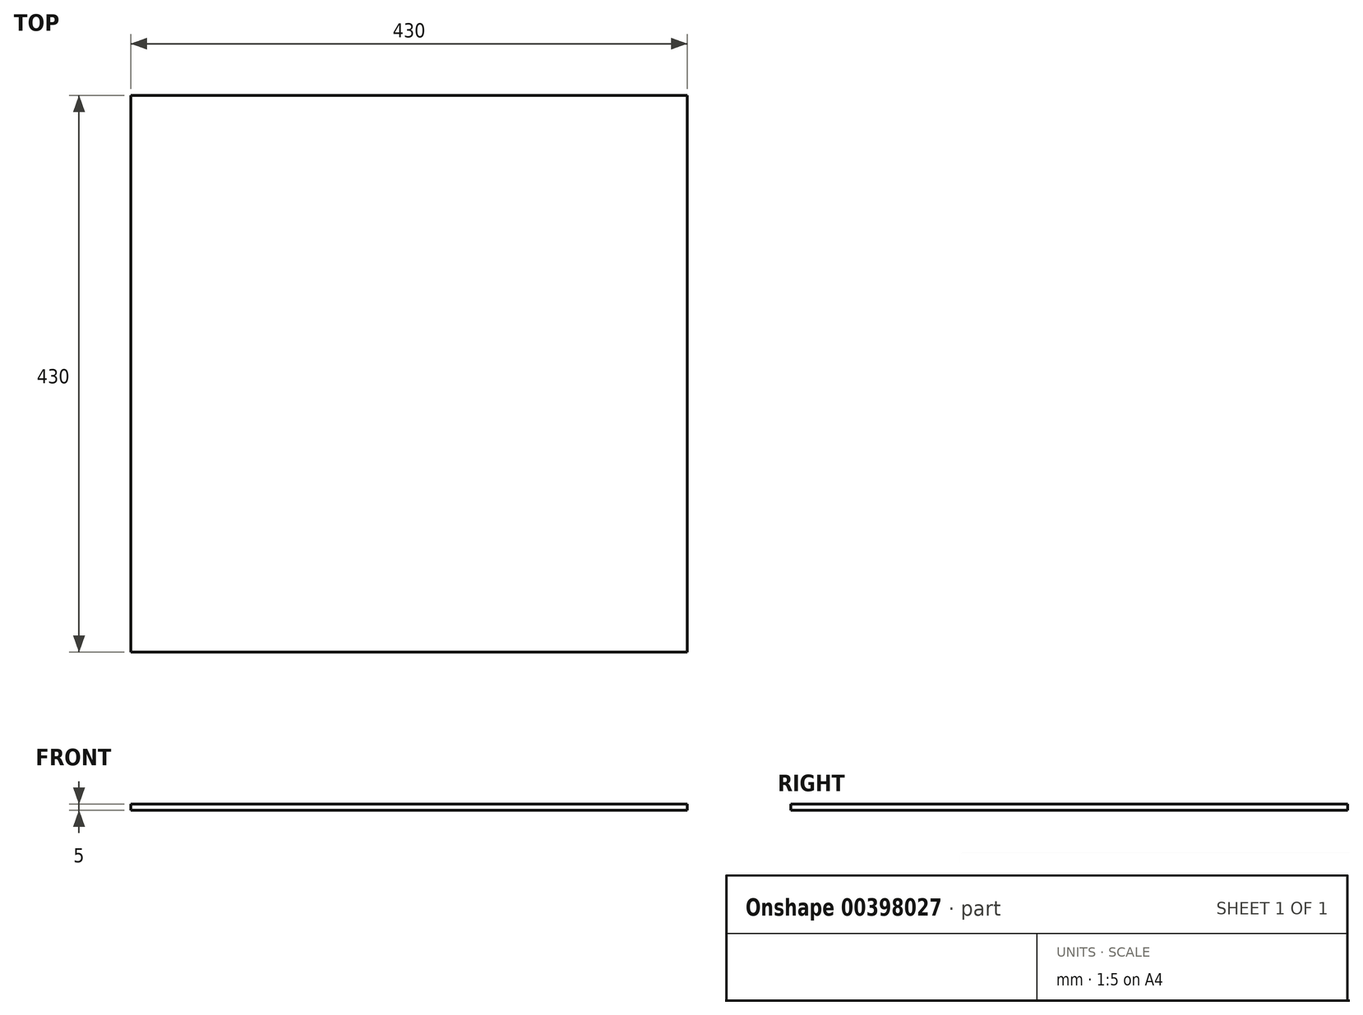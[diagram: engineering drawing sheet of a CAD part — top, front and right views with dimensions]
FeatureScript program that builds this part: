
annotation { "Feature Type Name" : "Feature", "Feature Type Description" : "" }
export const myFeature = defineFeature(function(context is Context, id is Id, definition is map)
    precondition{}
    {
        {
            var Q0;
            Q0=qCreatedBy(makeId("Top.planeOp"),FACE);
            var sketch = newSketch(context, id + "F0", { "sketchPlane" : qUnion([Q0])});
            skLineSegment(sketch, "E0.bottom", {"start": v(215, -215) * mm, "end": v(-215, -215) * mm});
            skLineSegment(sketch, "E0.top", {"start": v(215, 215) * mm, "end": v(-215, 215) * mm});
            skLineSegment(sketch, "E0.left", {"start": v(215, -215) * mm, "end": v(215, 215) * mm});
            skLineSegment(sketch, "E0.right", {"start": v(-215, -215) * mm, "end": v(-215, 215) * mm});
            skPoint(sketch, "E0.middle", {"position": v(0, 0) * mm});
            skSolve(sketch);
        }
        {
            var Q0;
            Q0 = qSketchRegion(id + "F0", true);
            extrude(context, id + "F1", {"entities" : qUnion([Q0]), "depth" : 5 * mm});
        }
    });
